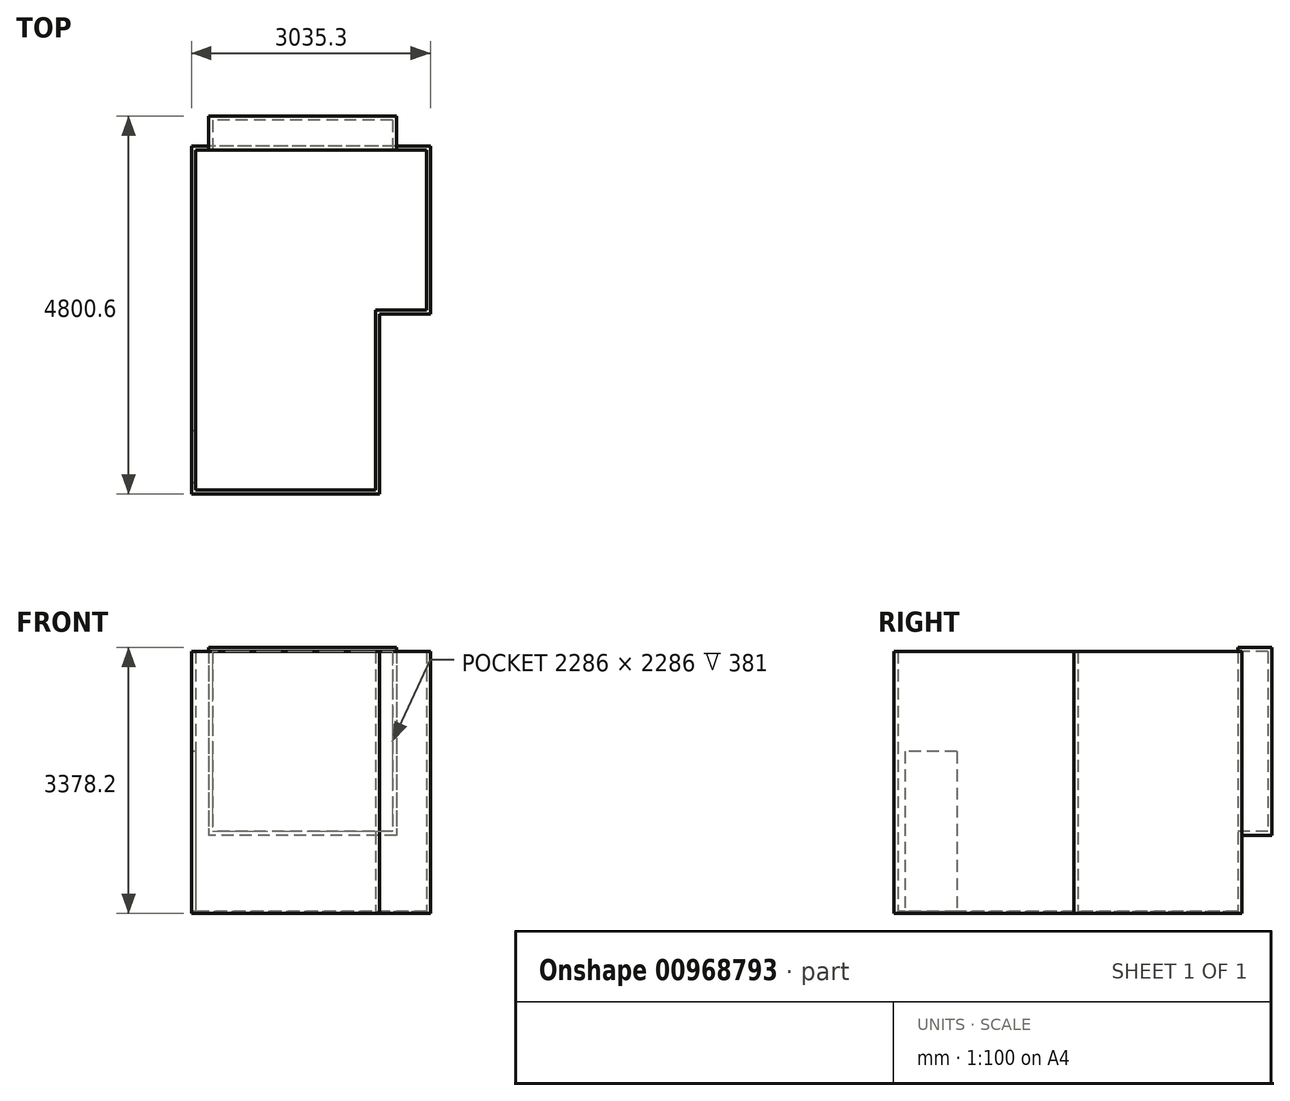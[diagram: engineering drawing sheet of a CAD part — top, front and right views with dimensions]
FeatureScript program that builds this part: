
annotation { "Feature Type Name" : "Feature", "Feature Type Description" : "" }
export const myFeature = defineFeature(function(context is Context, id is Id, definition is map)
    precondition{}
    {
        {
            var Q0;
            Q0=qCreatedBy(makeId("Top.planeOp"),FACE);
            var sketch = newSketch(context, id + "F0", { "sketchPlane" : qUnion([Q0])});
            skLineSegment(sketch, "E0", {"start": v(50.8, 4368.8) * mm, "end": v(50.8, 50.8) * mm});
            skLineSegment(sketch, "E1", {"start": v(50.8, 50.8) * mm, "end": v(2336.8, 50.8) * mm});
            skLineSegment(sketch, "E2", {"start": v(2336.8, 50.8) * mm, "end": v(2336.8, 2336.8) * mm});
            skLineSegment(sketch, "E3", {"start": v(2336.8, 2336.8) * mm, "end": v(2984.5, 2336.8) * mm});
            skLineSegment(sketch, "E4", {"start": v(2984.5, 2336.8) * mm, "end": v(2984.5, 4368.8) * mm});
            skLineSegment(sketch, "E5", {"start": v(2984.5, 4368.8) * mm, "end": v(50.8, 4368.8) * mm});
            skLineSegment(sketch, "E6", {"start": v(0, 4419.6) * mm, "end": v(0, 0) * mm});
            skLineSegment(sketch, "E7", {"start": v(0, 0) * mm, "end": v(2387.6, 0) * mm});
            skLineSegment(sketch, "E8", {"start": v(2387.6, 0) * mm, "end": v(2387.6, 2286) * mm});
            skLineSegment(sketch, "E9", {"start": v(2387.6, 2286) * mm, "end": v(3035.3, 2286) * mm});
            skLineSegment(sketch, "E10", {"start": v(3035.3, 2286) * mm, "end": v(3035.3, 4419.6) * mm});
            skLineSegment(sketch, "E11", {"start": v(3035.3, 4419.6) * mm, "end": v(0, 4419.6) * mm});
            skLineSegment(sketch, "E12", {"start": v(1193.8, 50.8) * mm, "end": v(1193.8, 0) * mm, "construction": true});
            skLineSegment(sketch, "E13", {"start": v(1517.65, 4368.8) * mm, "end": v(1517.65, 4419.6) * mm, "construction": true});
            skLineSegment(sketch, "E14", {"start": v(2984.5, 3352.8) * mm, "end": v(3035.3, 3352.8) * mm, "construction": true});
            skLineSegment(sketch, "E15", {"start": v(2336.8, 2286) * mm, "end": v(2387.6, 2286) * mm, "construction": true});
            skLineSegment(sketch, "E16", {"start": v(2362.2, 2336.8) * mm, "end": v(2362.2, 2286) * mm, "construction": true});
            skSolve(sketch);
        }
        {
            var Q0;
            Q0=makeQuery(id+"F0.imprint","IMPRINT",FACE,{"disambiguationData":[TD([[makeQuery(id+"F0.imprint","IMPRINT",EDGE,{"derivedFrom":sQuery(id+"F0.wireOp",EDGE,"E0")}),-1.0]])]});
            var sketch = newSketch(context, id + "F1", { "sketchPlane" : qUnion([Q0])});
            skLineSegment(sketch, "E17.top", {"start": v(0, 4419.6) * mm, "end": v(3035.3, 4419.6) * mm, "construction": true});
            skLineSegment(sketch, "E17.left", {"start": v(0, 0) * mm, "end": v(0, 4419.6) * mm});
            skLineSegment(sketch, "E18.bottom", {"start": v(0, 0) * mm, "end": v(2387.6, 0) * mm});
            skLineSegment(sketch, "E18.top", {"start": v(0, 4419.6) * mm, "end": v(3035.3, 4419.6) * mm});
            skLineSegment(sketch, "E19", {"start": v(3035.3, 4419.6) * mm, "end": v(3035.3, 2286) * mm});
            skLineSegment(sketch, "E20", {"start": v(3035.3, 2286) * mm, "end": v(2387.6, 2286) * mm});
            skLineSegment(sketch, "E21", {"start": v(2387.6, 2286) * mm, "end": v(2387.6, 0) * mm});
            skSolve(sketch);
        }
        {
            var Q0;
            Q0=qSketchRegion(id+"F0",true);
            extrude(context, id + "F2", {"entities" : qUnion([Q0]), "depth" : 3302 * mm, "offsetDistance" : 25.4 * mm});
        }
        {
            var Q0;
            Q0=qSketchRegion(id+"F1",true);
            extrude(context, id + "F3", {"entities" : qUnion([Q0]), "operationType" : NewBodyOperationType.ADD, "oppositeDirection" : true, "depth" : 25.4 * mm, "offsetDistance" : 25.4 * mm});
        }
        {
            var Q0;
            Q0=makeQuery(id+"F2.opExtrude","SWEPT_FACE",FACE,{"disambiguationData":[OSD([sQuery(id+"F0.wireOp",EDGE,"E6")])]});
            var sketch = newSketch(context, id + "F4", { "sketchPlane" : qUnion([Q0])});
            skLineSegment(sketch, "E22.bottom", {"start": v(-800.1, 2032) * mm, "end": v(-139.7, 2032) * mm});
            skLineSegment(sketch, "E22.top", {"start": v(-800.1, 0) * mm, "end": v(-139.7, 0) * mm});
            skLineSegment(sketch, "E22.left", {"start": v(-800.1, 2032) * mm, "end": v(-800.1, 0) * mm});
            skLineSegment(sketch, "E22.right", {"start": v(-139.7, 2032) * mm, "end": v(-139.7, 0) * mm});
            skLineSegment(sketch, "E23", {"start": v(-139.7, 2032) * mm, "end": v(0, 2032) * mm, "construction": true});
            skSolve(sketch);
        }
        {
            var Q0;
            Q0=qSketchRegion(id+"F4",true);
            extrude(context, id + "F5", {"entities" : qUnion([Q0]), "operationType" : NewBodyOperationType.REMOVE, "endBound" : BoundingType.UP_TO_NEXT, "oppositeDirection" : true, "depth" : 25.4 * mm, "offsetDistance" : 25.4 * mm});
        }
        {
            var Q0;
            Q0=makeQuery(id+"F2.opExtrude","SWEPT_FACE",FACE,{"disambiguationData":[OSD([sQuery(id+"F0.wireOp",EDGE,"E5")])]});
            var sketch = newSketch(context, id + "F6", { "sketchPlane" : qUnion([Q0])});
            skLineSegment(sketch, "E24", {"start": v(1409.7, 0) * mm, "end": v(1409.7, 1016) * mm, "construction": true});
            skLineSegment(sketch, "E25.bottom", {"start": v(2552.7, 3302) * mm, "end": v(266.7, 3302) * mm, "construction": true});
            skLineSegment(sketch, "E25.top", {"start": v(2552.7, 1016) * mm, "end": v(266.7, 1016) * mm, "construction": true});
            skLineSegment(sketch, "E25.left", {"start": v(2552.7, 3302) * mm, "end": v(2552.7, 1016) * mm, "construction": true});
            skLineSegment(sketch, "E25.right", {"start": v(266.7, 3302) * mm, "end": v(266.7, 1016) * mm, "construction": true});
            skLineSegment(sketch, "E26", {"start": v(50.8, 2159) * mm, "end": v(266.7, 2159) * mm});
            skLineSegment(sketch, "E27.bottom", {"start": v(2603.5, 3352.8) * mm, "end": v(215.9, 3352.8) * mm});
            skLineSegment(sketch, "E27.top", {"start": v(2603.5, 965.2) * mm, "end": v(215.9, 965.2) * mm});
            skLineSegment(sketch, "E27.left", {"start": v(215.9, 3352.8) * mm, "end": v(215.9, 965.2) * mm});
            skLineSegment(sketch, "E27.right", {"start": v(2603.5, 3352.8) * mm, "end": v(2603.5, 965.2) * mm});
            skLineSegment(sketch, "E28", {"start": v(1409.7, 965.2) * mm, "end": v(1409.7, 1016) * mm, "construction": true});
            skLineSegment(sketch, "E29", {"start": v(2552.7, 2159) * mm, "end": v(2603.5, 2159) * mm, "construction": true});
            skSolve(sketch);
        }
        {
            var Q0;
            Q0=qSketchRegion(id+"F6",true);
            extrude(context, id + "F7", {"entities" : qUnion([Q0]), "operationType" : NewBodyOperationType.ADD, "oppositeDirection" : true, "depth" : 431.8 * mm, "offsetDistance" : 25.4 * mm});
        }
        {
            var Q0;
            Q0=makeQuery(id+"F7.boolean.opBoolean","MERGE",FACE,{"derivedFrom":[makeQuery(id+"F2.opExtrude","SWEPT_FACE",FACE,{"disambiguationData":[OSD([sQuery(id+"F0.wireOp",EDGE,"E5")])]}),makeQuery(id+"F7.opExtrude","CAP_FACE",FACE,{"disambiguationData":[OSD([sQuery(id+"F6.wireOp",EDGE,"E27.bottom"),sQuery(id+"F6.wireOp",EDGE,"E27.top"),sQuery(id+"F6.wireOp",EDGE,"E27.left"),sQuery(id+"F6.wireOp",EDGE,"E27.right")])],"isStart":true})]});
            var sketch = newSketch(context, id + "F8", { "sketchPlane" : qUnion([Q0])});
            skLineSegment(sketch, "E30", {"start": v(1409.7, 0) * mm, "end": v(1409.7, 1016) * mm, "construction": true});
            skLineSegment(sketch, "E31.bottom", {"start": v(2552.7, 3302) * mm, "end": v(266.7, 3302) * mm});
            skLineSegment(sketch, "E31.top", {"start": v(2552.7, 1016) * mm, "end": v(266.7, 1016) * mm});
            skLineSegment(sketch, "E31.left", {"start": v(2552.7, 3302) * mm, "end": v(2552.7, 1016) * mm});
            skLineSegment(sketch, "E31.right", {"start": v(266.7, 3302) * mm, "end": v(266.7, 1016) * mm});
            skLineSegment(sketch, "E32", {"start": v(50.8, 2159) * mm, "end": v(266.7, 2159) * mm});
            skLineSegment(sketch, "E33.bottom", {"start": v(2603.5, 3352.8) * mm, "end": v(215.9, 3352.8) * mm, "construction": true});
            skLineSegment(sketch, "E33.top", {"start": v(2603.5, 965.2) * mm, "end": v(215.9, 965.2) * mm, "construction": true});
            skLineSegment(sketch, "E33.left", {"start": v(215.9, 3352.8) * mm, "end": v(215.9, 965.2) * mm, "construction": true});
            skLineSegment(sketch, "E33.right", {"start": v(2603.5, 3352.8) * mm, "end": v(2603.5, 965.2) * mm, "construction": true});
            skLineSegment(sketch, "E34", {"start": v(1409.7, 965.2) * mm, "end": v(1409.7, 1016) * mm, "construction": true});
            skLineSegment(sketch, "E35", {"start": v(2552.7, 2159) * mm, "end": v(2603.5, 2159) * mm, "construction": true});
            skSolve(sketch);
        }
        {
            var Q0;
            Q0=qSketchRegion(id+"F8",true);
            extrude(context, id + "F9", {"entities" : qUnion([Q0]), "operationType" : NewBodyOperationType.REMOVE, "oppositeDirection" : true, "depth" : 381 * mm, "offsetDistance" : 25.4 * mm});
        }
    });
